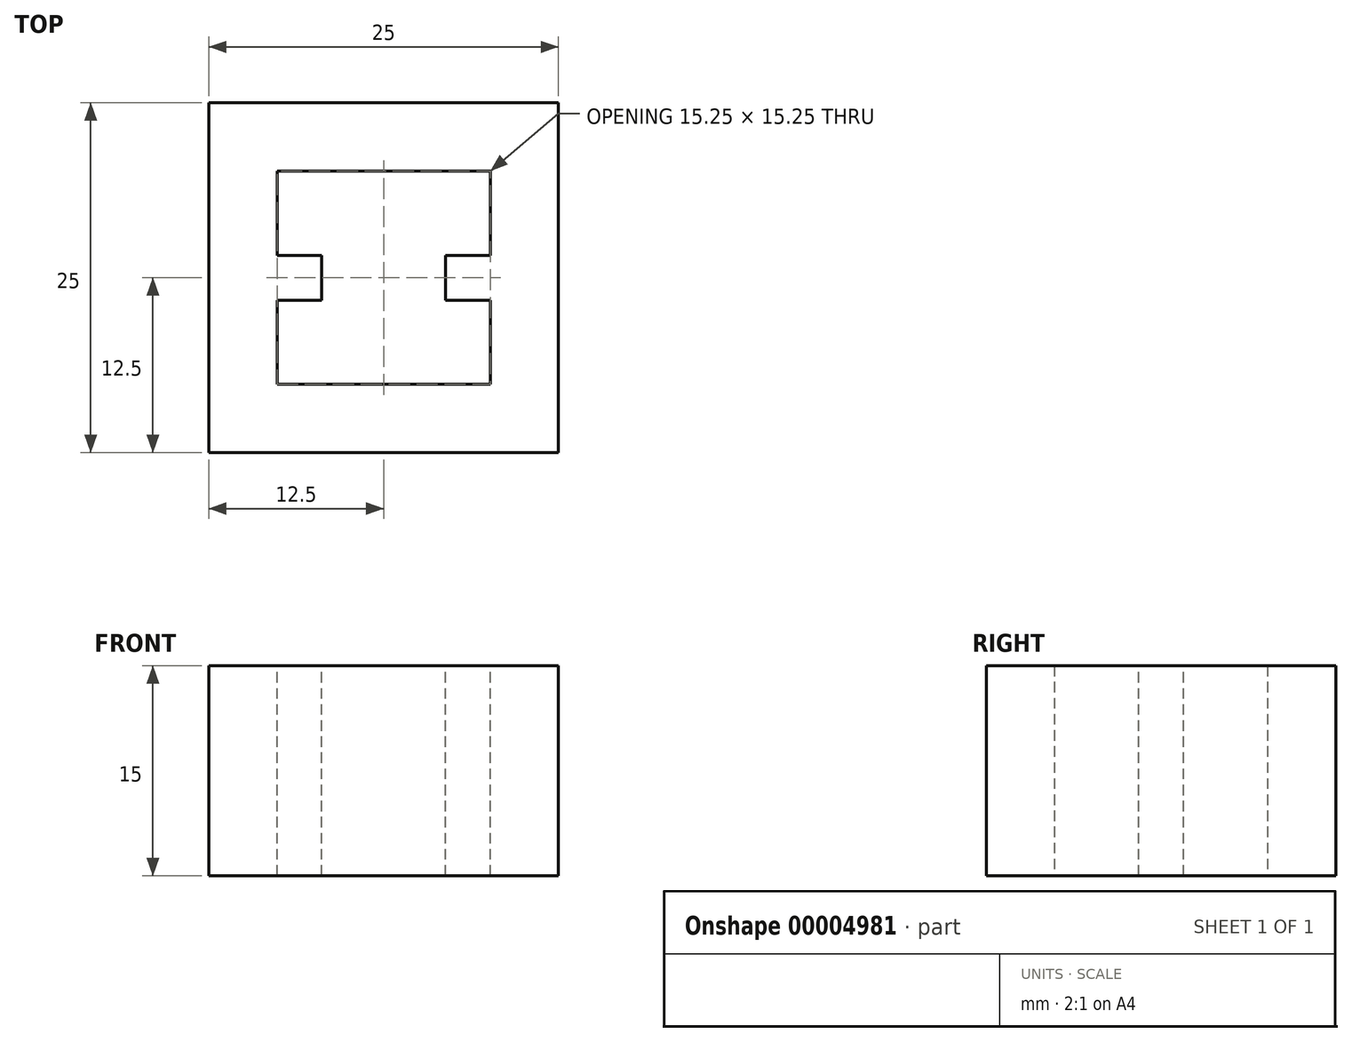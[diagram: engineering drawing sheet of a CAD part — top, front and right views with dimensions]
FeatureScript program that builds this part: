
annotation { "Feature Type Name" : "Feature", "Feature Type Description" : "" }
export const myFeature = defineFeature(function(context is Context, id is Id, definition is map)
    precondition{}
    {
        {
            var Q0;
            Q0=qCreatedBy(makeId("Top.planeOp"),FACE);
            var sketch = newSketch(context, id + "F0", { "sketchPlane" : qUnion([Q0])});
            skLineSegment(sketch, "E0.rect.bottom", {"start": v(12.5, 12.5) * mm, "end": v(-12.5, 12.5) * mm});
            skLineSegment(sketch, "E0.rect.top", {"start": v(12.5, -12.5) * mm, "end": v(-12.5, -12.5) * mm});
            skLineSegment(sketch, "E0.rect.left", {"start": v(12.5, 12.5) * mm, "end": v(12.5, -12.5) * mm});
            skLineSegment(sketch, "E0.rect.right", {"start": v(-12.5, 12.5) * mm, "end": v(-12.5, -12.5) * mm});
            skPoint(sketch, "E0.rect.middle", {"position": v(0, 0) * mm});
            skLineSegment(sketch, "E1.rect.bottom", {"start": v(7.62, 7.62) * mm, "end": v(-7.63, 7.62) * mm});
            skLineSegment(sketch, "E1.rect.top", {"start": v(7.63, -7.63) * mm, "end": v(-7.62, -7.63) * mm});
            skLineSegment(sketch, "E1.rect.left", {"start": v(7.62, 7.62) * mm, "end": v(7.63, -7.63) * mm});
            skLineSegment(sketch, "E1.rect.right", {"start": v(-7.63, 7.62) * mm, "end": v(-7.62, -7.63) * mm});
            skSolve(sketch);
        }
        {
            var Q0;
            Q0 = qSketchRegion(id + "F0", true);
            extrude(context, id + "F1", {"entities" : qUnion([Q0]), "depth" : 15 * mm});
        }
        {
            var Q0;
            Q0=makeQuery(id+"F1.opExtrude","CAP_FACE",FACE,{"disambiguationData":[OSD([sQuery(id+"F0.wireOp",EDGE,"E0.rect.bottom"),sQuery(id+"F0.wireOp",EDGE,"E0.rect.top"),sQuery(id+"F0.wireOp",EDGE,"E0.rect.left"),sQuery(id+"F0.wireOp",EDGE,"E0.rect.right"),sQuery(id+"F0.wireOp",EDGE,"E1.rect.bottom"),sQuery(id+"F0.wireOp",EDGE,"E1.rect.top"),sQuery(id+"F0.wireOp",EDGE,"E1.rect.left"),sQuery(id+"F0.wireOp",EDGE,"E1.rect.right")])],"isStart":false});
            var sketch = newSketch(context, id + "F2", { "sketchPlane" : qUnion([Q0])});
            skLineSegment(sketch, "E2", {"start": v(-7.62, 0) * mm, "end": v(7.62, 0) * mm, "construction": true});
            skLineSegment(sketch, "E3.bottom", {"start": v(-7.62, 1.6) * mm, "end": v(-4.42, 1.6) * mm});
            skLineSegment(sketch, "E3.top", {"start": v(-7.62, -1.6) * mm, "end": v(-4.42, -1.6) * mm});
            skLineSegment(sketch, "E3.left", {"start": v(-7.62, 1.6) * mm, "end": v(-7.62, -1.6) * mm});
            skLineSegment(sketch, "E3.right", {"start": v(-4.42, 1.6) * mm, "end": v(-4.42, -1.6) * mm});
            skPoint(sketch, "E4", {"position": v(-4.42, 0) * mm});
            skLineSegment(sketch, "E5", {"start": v(0, 7.62) * mm, "end": v(0, -7.62) * mm, "construction": true});
            skLineSegment(sketch, "E6.0.MirrorCS", {"start": v(7.63, -1.6) * mm, "end": v(4.43, -1.6) * mm});
            skLineSegment(sketch, "E6.1.MirrorCS", {"start": v(7.62, 1.6) * mm, "end": v(7.63, -1.6) * mm});
            skLineSegment(sketch, "E6.2.MirrorCS", {"start": v(4.42, 1.6) * mm, "end": v(4.43, -1.6) * mm});
            skLineSegment(sketch, "E6.3.MirrorCS", {"start": v(7.62, 1.6) * mm, "end": v(4.42, 1.6) * mm});
            skSolve(sketch);
        }
        {
            var Q0;
            Q0 = qSketchRegion(id + "F2", true);
            var Q1;
            Q1=makeQuery(id+"F1.opExtrude","CAP_FACE",FACE,{"disambiguationData":[OSD([sQuery(id+"F0.wireOp",EDGE,"E0.rect.bottom"),sQuery(id+"F0.wireOp",EDGE,"E0.rect.top"),sQuery(id+"F0.wireOp",EDGE,"E0.rect.left"),sQuery(id+"F0.wireOp",EDGE,"E0.rect.right"),sQuery(id+"F0.wireOp",EDGE,"E1.rect.bottom"),sQuery(id+"F0.wireOp",EDGE,"E1.rect.top"),sQuery(id+"F0.wireOp",EDGE,"E1.rect.left"),sQuery(id+"F0.wireOp",EDGE,"E1.rect.right")])],"isStart":true});
            extrude(context, id + "F3", {"entities" : qUnion([Q0]), "operationType" : NewBodyOperationType.ADD, "endBound" : BoundingType.UP_TO_SURFACE, "oppositeDirection" : true, "endBoundEntityFace" : qUnion([Q1]), "depth" : 25 * mm});
        }
    });
